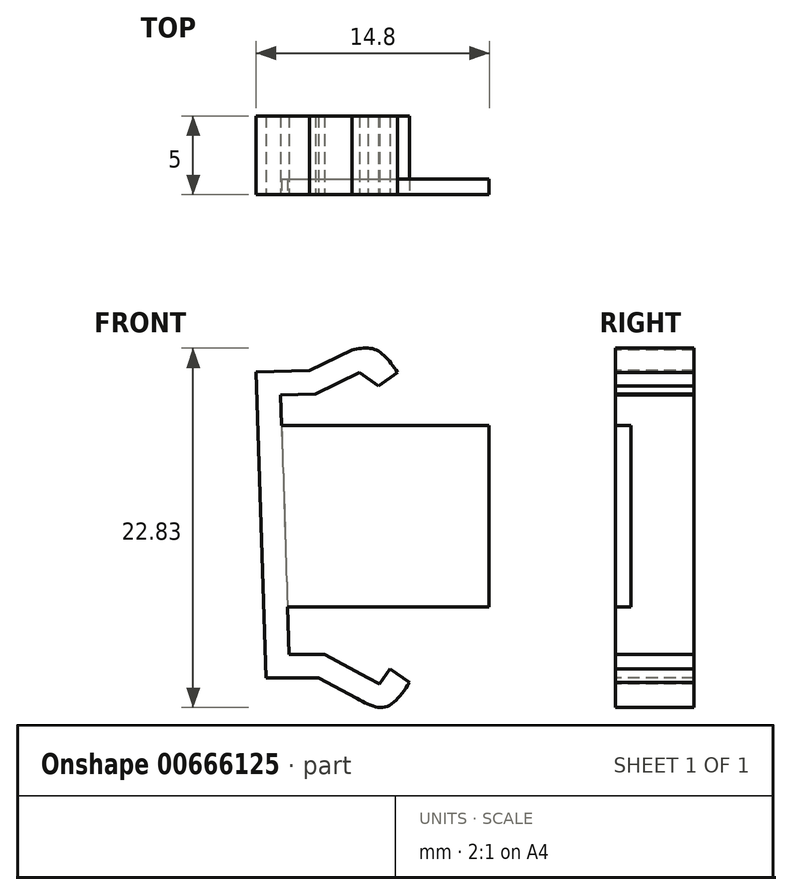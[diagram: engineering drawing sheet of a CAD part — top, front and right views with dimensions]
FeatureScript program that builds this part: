
annotation { "Feature Type Name" : "Feature", "Feature Type Description" : "" }
export const myFeature = defineFeature(function(context is Context, id is Id, definition is map)
    precondition{}
    {
        {
            var Q0;
            Q0=qCreatedBy(makeId("Front.planeOp"),FACE);
            var sketch = newSketch(context, id + "F0", { "sketchPlane" : qUnion([Q0])});
            skLineSegment(sketch, "E0", {"start": v(-18.46, 1.53) * mm, "end": v(-17.83, -17.9) * mm});
            skLineSegment(sketch, "E1", {"start": v(-17.83, -17.9) * mm, "end": v(-14.5, -17.9) * mm});
            skLineSegment(sketch, "E2", {"start": v(-18.46, 1.53) * mm, "end": v(-15.08, 1.64) * mm});
            skLineSegment(sketch, "E3", {"start": v(-15.08, 1.64) * mm, "end": v(-12.38, 2.94) * mm});
            skLineSegment(sketch, "E4", {"start": v(-14.5, -17.9) * mm, "end": v(-12.06, -19.2) * mm});
            skFitSpline(sketch, "E5", {"points": [v(-12.38, 2.94) * mm, v(-10.86, 2.94) * mm, v(-9.48, 1.5) * mm], "startDerivative": vector(3.41, 0.63) * mm, "endDerivative": vector(2.42, -3.4) * mm});
            skFitSpline(sketch, "E6", {"points": [v(-12.06, -19.2) * mm, v(-10.28, -19.75) * mm, v(-8.72, -18.18) * mm], "startDerivative": vector(3.9, -2.12) * mm, "endDerivative": vector(2.8, 4.07) * mm});
            skLineSegment(sketch, "E7.1", {"start": v(-14.71, 0.15) * mm, "end": v(-11.92, 1.5) * mm});
            skLineSegment(sketch, "E7.2", {"start": v(-16.92, 0.08) * mm, "end": v(-14.71, 0.15) * mm});
            skLineSegment(sketch, "E7.4", {"start": v(-14.11, -16.4) * mm, "end": v(-11.35, -17.89) * mm});
            skLineSegment(sketch, "E7.5", {"start": v(-16.38, -16.4) * mm, "end": v(-14.11, -16.4) * mm});
            skLineSegment(sketch, "E7.6", {"start": v(-16.92, 0.08) * mm, "end": v(-16.38, -16.4) * mm});
            skLineSegment(sketch, "E8", {"start": v(-10.7, 0.64) * mm, "end": v(-9.48, 1.5) * mm});
            skLineSegment(sketch, "E9", {"start": v(-9.95, -17.33) * mm, "end": v(-8.72, -18.18) * mm});
            skLineSegment(sketch, "E10", {"start": v(-11.92, 1.5) * mm, "end": v(-11.92, 1.5) * mm});
            skLineSegment(sketch, "E11", {"start": v(-11.92, 1.5) * mm, "end": v(-10.7, 0.64) * mm});
            skLineSegment(sketch, "E12", {"start": v(-11.35, -17.89) * mm, "end": v(-10.64, -18.3) * mm});
            skLineSegment(sketch, "E13", {"start": v(-10.64, -18.3) * mm, "end": v(-9.95, -17.33) * mm});
            skSolve(sketch);
        }
        {
            var Q0;
            Q0=makeQuery(id+"F0.imprint","IMPRINT",FACE,{"disambiguationData":[TD([[makeQuery(id+"F0.imprint","IMPRINT",EDGE,{"derivedFrom":sQuery(id+"F0.wireOp",EDGE,"E0")}),1.0]])]});
            extrude(context, id + "F1", {"entities" : qUnion([Q0]), "oppositeDirection" : true, "depth" : 5 * mm, "offsetDistance" : 25 * mm});
        }
        {
            var Q0;
            Q0=makeQuery(id+"F0.imprint","IMPRINT",FACE,{"disambiguationData":[TD([[makeQuery(id+"F0.imprint","IMPRINT",EDGE,{"derivedFrom":sQuery(id+"F0.wireOp",EDGE,"E0")}),1.0]])]});
            var sketch = newSketch(context, id + "F2", { "sketchPlane" : qUnion([Q0])});
            skLineSegment(sketch, "E14.bottom", {"start": v(-17.64, -1.85) * mm, "end": v(-3.66, -1.85) * mm});
            skLineSegment(sketch, "E14.top", {"start": v(-17.64, -13.37) * mm, "end": v(-3.66, -13.37) * mm});
            skLineSegment(sketch, "E14.left", {"start": v(-17.64, -1.85) * mm, "end": v(-17.64, -13.37) * mm});
            skLineSegment(sketch, "E14.right", {"start": v(-3.66, -1.85) * mm, "end": v(-3.66, -13.37) * mm});
            skSolve(sketch);
        }
        {
            var Q0;
            {var subQ0=sQuery(id+"F2.wireOp",EDGE,"E14.right");Q0=makeQuery(id+"F2.imprint","IMPRINT",FACE,{"disambiguationData":[TD([[makeQuery(id+"F2.imprint","IMPRINT",EDGE,{"derivedFrom":subQ0}),-1.0]])]});}
            extrude(context, id + "F3", {"entities" : qUnion([Q0]), "operationType" : NewBodyOperationType.ADD, "oppositeDirection" : true, "depth" : 1 * mm, "offsetDistance" : 25 * mm});
        }
        {
            var Q0;
            Q0=makeQuery(id+"F1.opExtrude","SWEPT_BODY",BODY,{"disambiguationData":[OSD([sQuery(id+"F0.wireOp",EDGE,"E0"),sQuery(id+"F0.wireOp",EDGE,"E1"),sQuery(id+"F0.wireOp",EDGE,"E2"),sQuery(id+"F0.wireOp",EDGE,"E3"),sQuery(id+"F0.wireOp",EDGE,"E4"),sQuery(id+"F0.wireOp",EDGE,"E5"),sQuery(id+"F0.wireOp",EDGE,"E6"),sQuery(id+"F0.wireOp",EDGE,"E7.1"),sQuery(id+"F0.wireOp",EDGE,"E7.2"),sQuery(id+"F0.wireOp",EDGE,"E7.4"),sQuery(id+"F0.wireOp",EDGE,"E7.5"),sQuery(id+"F0.wireOp",EDGE,"E7.6"),sQuery(id+"F0.wireOp",EDGE,"E8"),sQuery(id+"F0.wireOp",EDGE,"E9"),sQuery(id+"F0.wireOp",EDGE,"E11"),sQuery(id+"F0.wireOp",EDGE,"E12"),sQuery(id+"F0.wireOp",EDGE,"E13")])]});
            var Q1;
            Q1=makeQuery(id+"F3.opExtrude","CAP_VERTEX",VERTEX,{"disambiguationData":[OSD([sQuery(id+"F2.wireOp",EDGE,"E14.bottom"),sQuery(id+"F2.wireOp",EDGE,"E14.right")])],"isStart":false});
            transform(context, id + "F4", {"entities" : qUnion([Q0]), "transformType" : TransformType.SCALE_UNIFORMLY, "scale" : 1, "scalePoint" : qUnion([Q1]), "makeCopy" : true});
        }
    });
